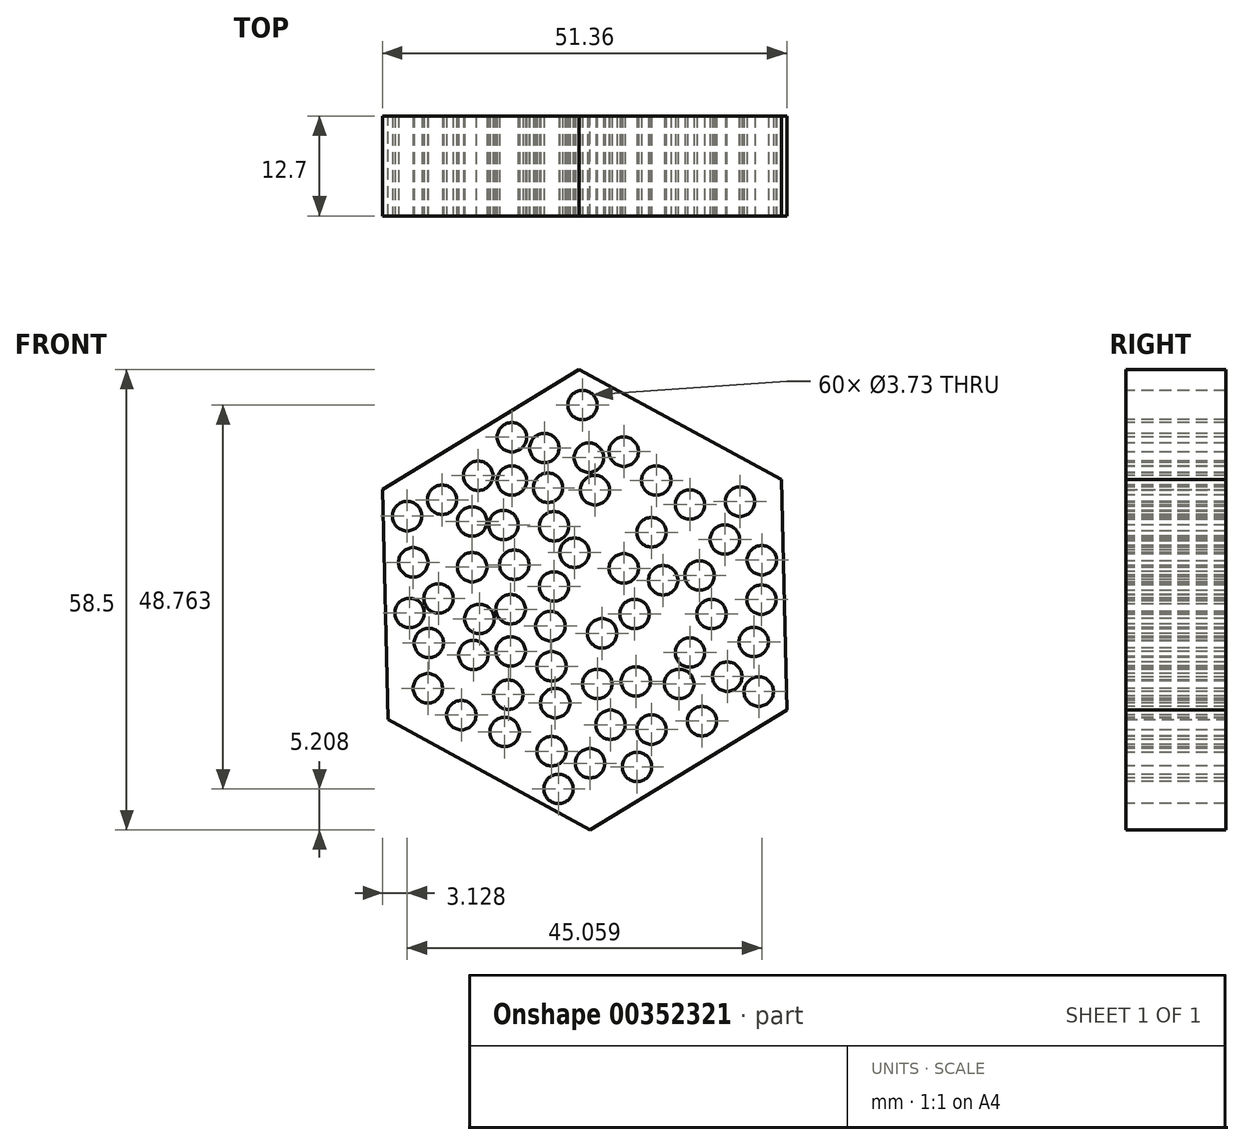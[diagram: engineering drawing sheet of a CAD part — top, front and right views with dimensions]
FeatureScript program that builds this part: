
annotation { "Feature Type Name" : "Feature", "Feature Type Description" : "" }
export const myFeature = defineFeature(function(context is Context, id is Id, definition is map)
    precondition{}
    {
        {
            var Q0;
            Q0=qCreatedBy(makeId("Front.planeOp"),FACE);
            var sketch = newSketch(context, id + "F0", { "sketchPlane" : qUnion([Q0])});
            skCircle(sketch, "E0.cCircle", {"center": v(0, 0) * mm, "radius": 25.34 * mm, "construction": true});
            skLineSegment(sketch, "E0.0", {"start": v(-25.68, 14.02) * mm, "end": v(-0.7, 29.25) * mm});
            skLineSegment(sketch, "E0.1", {"start": v(-0.7, 29.25) * mm, "end": v(24.98, 15.23) * mm});
            skLineSegment(sketch, "E0.2", {"start": v(24.98, 15.23) * mm, "end": v(25.68, -14.02) * mm});
            skLineSegment(sketch, "E0.3", {"start": v(25.68, -14.02) * mm, "end": v(0.7, -29.25) * mm});
            skLineSegment(sketch, "E0.4", {"start": v(0.7, -29.25) * mm, "end": v(-24.98, -15.23) * mm});
            skLineSegment(sketch, "E0.5", {"start": v(-24.98, -15.23) * mm, "end": v(-25.68, 14.02) * mm});
            skPoint(sketch, "E0.0.midPoint", {"position": v(-13.2, 21.64) * mm});
            skSolve(sketch);
        }
        {
            var Q0;
            Q0 = qSketchRegion(id + "F0", true);
            extrude(context, id + "F1", {"entities" : qUnion([Q0]), "depth" : 12.7 * mm});
        }
        {
            var Q0;
            Q0=makeQuery(id+"F1.opExtrude","CAP_FACE",FACE,{"disambiguationData":[OSD([sQuery(id+"F0.wireOp",EDGE,"E0.0"),sQuery(id+"F0.wireOp",EDGE,"E0.1"),sQuery(id+"F0.wireOp",EDGE,"E0.2"),sQuery(id+"F0.wireOp",EDGE,"E0.3"),sQuery(id+"F0.wireOp",EDGE,"E0.4"),sQuery(id+"F0.wireOp",EDGE,"E0.5")])],"isStart":false});
            var sketch = newSketch(context, id + "F2", { "sketchPlane" : qUnion([Q0])});
            skCircle(sketch, "E1", {"center": v(-22.55, 10.6) * mm, "radius": 1.87 * mm});
            skCircle(sketch, "E2", {"center": v(-19.92, -11.27) * mm, "radius": 1.87 * mm});
            skCircle(sketch, "E3", {"center": v(-3.32, -24.04) * mm, "radius": 1.87 * mm});
            skCircle(sketch, "E4", {"center": v(-4.2, -8.47) * mm, "radius": 1.87 * mm});
            skCircle(sketch, "E5", {"center": v(9.97, 2.46) * mm, "radius": 1.87 * mm});
            skCircle(sketch, "E6", {"center": v(22.11, -11.68) * mm, "radius": 1.87 * mm});
            skCircle(sketch, "E7", {"center": v(21.48, -5.38) * mm, "radius": 1.87 * mm});
            skCircle(sketch, "E8", {"center": v(22.46, 0) * mm, "radius": 1.87 * mm});
            skCircle(sketch, "E9", {"center": v(22.5, 5.01) * mm, "radius": 1.87 * mm});
            skCircle(sketch, "E10", {"center": v(19.73, 12.45) * mm, "radius": 1.87 * mm});
            skCircle(sketch, "E11", {"center": v(-0.27, 24.72) * mm, "radius": 1.87 * mm});
            skCircle(sketch, "E12", {"center": v(-9.25, 20.63) * mm, "radius": 1.87 * mm});
            skCircle(sketch, "E13", {"center": v(-9.25, 15.13) * mm, "radius": 1.87 * mm});
            skCircle(sketch, "E14", {"center": v(-10.32, 9.48) * mm, "radius": 1.87 * mm});
            skCircle(sketch, "E15", {"center": v(-8.94, 4.43) * mm, "radius": 1.87 * mm});
            skCircle(sketch, "E16", {"center": v(-9.4, -1.22) * mm, "radius": 1.87 * mm});
            skCircle(sketch, "E17", {"center": v(-9.4, -6.57) * mm, "radius": 1.87 * mm});
            skCircle(sketch, "E18", {"center": v(-9.7, -12.07) * mm, "radius": 1.87 * mm});
            skCircle(sketch, "E19", {"center": v(-10.16, -16.81) * mm, "radius": 1.87 * mm});
            skCircle(sketch, "E20", {"center": v(-15.67, -14.67) * mm, "radius": 1.87 * mm});
            skCircle(sketch, "E21", {"center": v(-14.14, -7.03) * mm, "radius": 1.87 * mm});
            skCircle(sketch, "E22", {"center": v(-13.37, -2.45) * mm, "radius": 1.87 * mm});
            skCircle(sketch, "E23", {"center": v(-14.3, 4.13) * mm, "radius": 1.87 * mm});
            skCircle(sketch, "E24", {"center": v(-14.3, 9.93) * mm, "radius": 1.87 * mm});
            skCircle(sketch, "E25", {"center": v(-13.53, 15.74) * mm, "radius": 1.87 * mm});
            skCircle(sketch, "E26", {"center": v(-18.11, 12.69) * mm, "radius": 1.87 * mm});
            skCircle(sketch, "E27", {"center": v(-21.78, 4.74) * mm, "radius": 1.87 * mm});
            skCircle(sketch, "E28", {"center": v(-18.57, 0.15) * mm, "radius": 1.87 * mm});
            skCircle(sketch, "E29", {"center": v(-19.8, -5.5) * mm, "radius": 1.87 * mm});
            skCircle(sketch, "E30", {"center": v(-22.24, -1.68) * mm, "radius": 1.87 * mm});
            skCircle(sketch, "E31", {"center": v(-5.12, 19.26) * mm, "radius": 1.87 * mm});
            skCircle(sketch, "E32", {"center": v(-4.66, 14.21) * mm, "radius": 1.87 * mm});
            skCircle(sketch, "E33", {"center": v(-3.9, 9.32) * mm, "radius": 1.87 * mm});
            skCircle(sketch, "E34", {"center": v(-1.3, 5.96) * mm, "radius": 1.87 * mm});
            skCircle(sketch, "E35", {"center": v(4.97, 3.97) * mm, "radius": 1.87 * mm});
            skCircle(sketch, "E36", {"center": v(14.6, 3.06) * mm, "radius": 1.87 * mm});
            skCircle(sketch, "E37", {"center": v(17.8, 7.64) * mm, "radius": 1.87 * mm});
            skCircle(sketch, "E38", {"center": v(13.37, 12.07) * mm, "radius": 1.87 * mm});
            skCircle(sketch, "E39", {"center": v(9.1, 15.13) * mm, "radius": 1.87 * mm});
            skCircle(sketch, "E40", {"center": v(4.97, 18.8) * mm, "radius": 1.87 * mm});
            skCircle(sketch, "E41", {"center": v(0.53, 18.03) * mm, "radius": 1.87 * mm});
            skCircle(sketch, "E42", {"center": v(1.3, 13.9) * mm, "radius": 1.87 * mm});
            skCircle(sketch, "E43", {"center": v(8.48, 8.56) * mm, "radius": 1.87 * mm});
            skCircle(sketch, "E44", {"center": v(-3.9, 1.68) * mm, "radius": 1.87 * mm});
            skCircle(sketch, "E45", {"center": v(-4.36, -3.36) * mm, "radius": 1.87 * mm});
            skCircle(sketch, "E46", {"center": v(-3.74, -13.14) * mm, "radius": 1.87 * mm});
            skCircle(sketch, "E47", {"center": v(-4.2, -19.26) * mm, "radius": 1.87 * mm});
            skCircle(sketch, "E48", {"center": v(0.69, -20.79) * mm, "radius": 1.87 * mm});
            skCircle(sketch, "E49", {"center": v(6.65, -21.24) * mm, "radius": 1.87 * mm});
            skCircle(sketch, "E50", {"center": v(14.9, -15.44) * mm, "radius": 1.87 * mm});
            skCircle(sketch, "E51", {"center": v(18.11, -9.78) * mm, "radius": 1.87 * mm});
            skCircle(sketch, "E52", {"center": v(16.12, -1.83) * mm, "radius": 1.87 * mm});
            skCircle(sketch, "E53", {"center": v(6.34, -1.83) * mm, "radius": 1.87 * mm});
            skCircle(sketch, "E54", {"center": v(2.22, -4.28) * mm, "radius": 1.87 * mm});
            skCircle(sketch, "E55", {"center": v(1.6, -10.7) * mm, "radius": 1.87 * mm});
            skCircle(sketch, "E56", {"center": v(3.29, -15.9) * mm, "radius": 1.87 * mm});
            skCircle(sketch, "E57", {"center": v(8.48, -16.5) * mm, "radius": 1.87 * mm});
            skCircle(sketch, "E58", {"center": v(12, -10.7) * mm, "radius": 1.87 * mm});
            skCircle(sketch, "E59", {"center": v(6.5, -10.4) * mm, "radius": 1.87 * mm});
            skCircle(sketch, "E60", {"center": v(13.37, -6.72) * mm, "radius": 1.87 * mm});
            skSolve(sketch);
        }
        {
            var Q0;
            Q0 = qSketchRegion(id + "F2", true);
            extrude(context, id + "F3", {"entities" : qUnion([Q0]), "operationType" : NewBodyOperationType.REMOVE, "oppositeDirection" : true, "depth" : 14.48 * mm});
        }
    });
